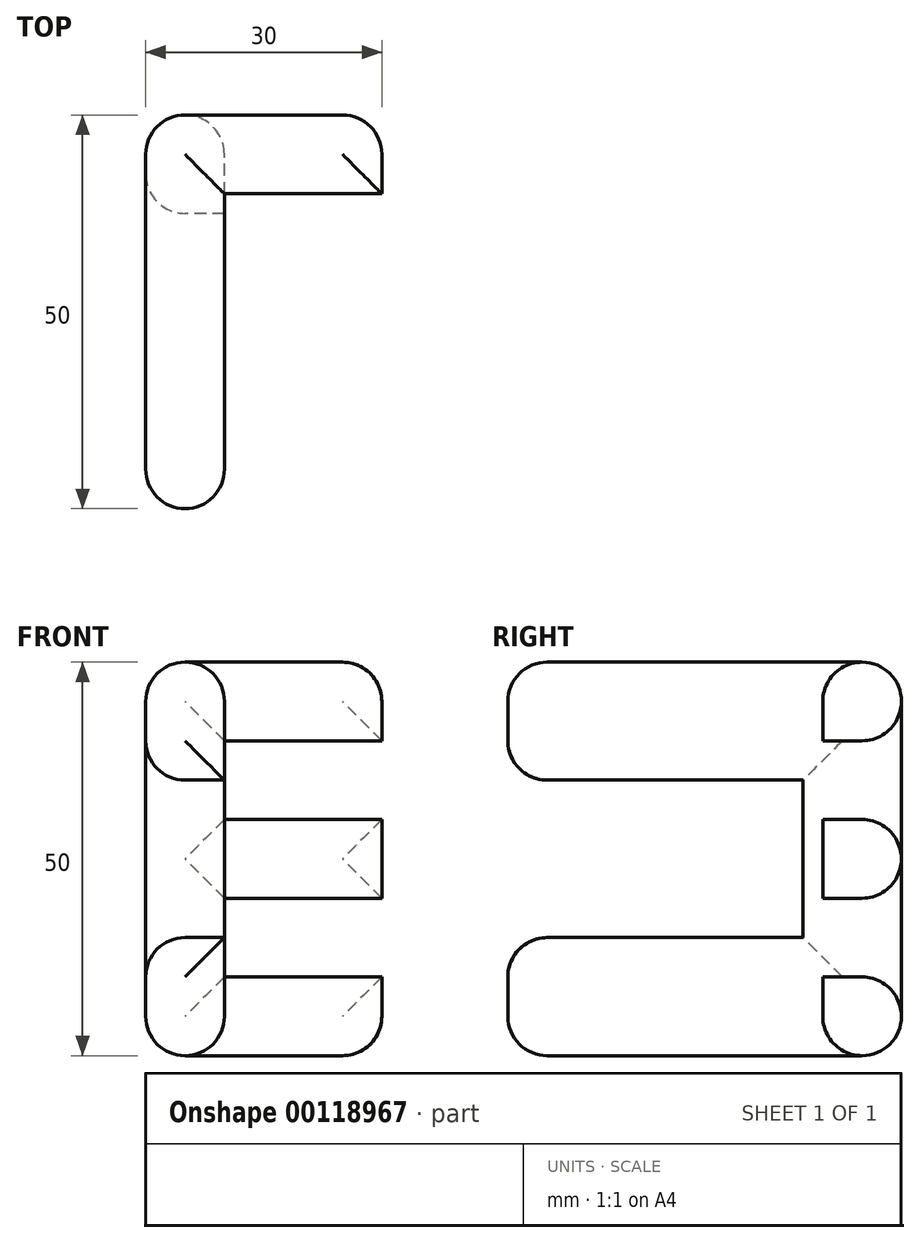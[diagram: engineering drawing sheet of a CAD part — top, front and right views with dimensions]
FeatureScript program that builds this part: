
annotation { "Feature Type Name" : "Feature", "Feature Type Description" : "" }
export const myFeature = defineFeature(function(context is Context, id is Id, definition is map)
    precondition{}
    {
        {
            var Q0;
            Q0=qCreatedBy(makeId("Front.planeOp"),FACE);
            var sketch = newSketch(context, id + "F0", { "sketchPlane" : qUnion([Q0])});
            skLineSegment(sketch, "E0.bottom", {"start": v(25, 25) * mm, "end": v(-25, 25) * mm, "construction": true});
            skLineSegment(sketch, "E0.top", {"start": v(25, -25) * mm, "end": v(-25, -25) * mm, "construction": true});
            skLineSegment(sketch, "E0.left", {"start": v(25, 25) * mm, "end": v(25, -25) * mm, "construction": true});
            skLineSegment(sketch, "E0.right", {"start": v(-25, 25) * mm, "end": v(-25, -25) * mm, "construction": true});
            skPoint(sketch, "E0.middle", {"position": v(0, 0) * mm});
            skLineSegment(sketch, "E1", {"start": v(-15, 25) * mm, "end": v(-15, -25) * mm, "construction": true});
            skLineSegment(sketch, "E2", {"start": v(-5, 25) * mm, "end": v(-5, -25) * mm, "construction": true});
            skLineSegment(sketch, "E3", {"start": v(5, 25) * mm, "end": v(5, -25) * mm, "construction": true});
            skLineSegment(sketch, "E4", {"start": v(15, 25) * mm, "end": v(15, -25) * mm, "construction": true});
            skLineSegment(sketch, "E5", {"start": v(-25, 15) * mm, "end": v(25, 15) * mm, "construction": true});
            skLineSegment(sketch, "E6", {"start": v(-25, 5) * mm, "end": v(25, 5) * mm, "construction": true});
            skLineSegment(sketch, "E7", {"start": v(-25, -5) * mm, "end": v(25, -5) * mm, "construction": true});
            skLineSegment(sketch, "E8", {"start": v(-25, -15) * mm, "end": v(25, -15) * mm, "construction": true});
            skLineSegment(sketch, "E9", {"start": v(-15, 25) * mm, "end": v(-15, -25) * mm});
            skLineSegment(sketch, "E10", {"start": v(15, -25) * mm, "end": v(15, -15) * mm});
            skLineSegment(sketch, "E11", {"start": v(15, -15) * mm, "end": v(-5, -15) * mm});
            skLineSegment(sketch, "E12", {"start": v(-5, -15) * mm, "end": v(-5, -5) * mm});
            skLineSegment(sketch, "E13", {"start": v(-5, -5) * mm, "end": v(15, -5) * mm});
            skLineSegment(sketch, "E14", {"start": v(15, -5) * mm, "end": v(15, 5) * mm});
            skLineSegment(sketch, "E15", {"start": v(15, 5) * mm, "end": v(-5, 5) * mm});
            skLineSegment(sketch, "E16", {"start": v(-5, 5) * mm, "end": v(-5, 15) * mm});
            skLineSegment(sketch, "E17", {"start": v(-5, 15) * mm, "end": v(15, 15) * mm});
            skLineSegment(sketch, "E18", {"start": v(15, 15) * mm, "end": v(15, 25) * mm});
            skLineSegment(sketch, "E19", {"start": v(15, 25) * mm, "end": v(-15, 25) * mm});
            skLineSegment(sketch, "E20", {"start": v(15, -25) * mm, "end": v(-15, -25) * mm});
            skSolve(sketch);
        }
        {
            var Q0;
            Q0=qCreatedBy(makeId("Top.planeOp"),FACE);
            var sketch = newSketch(context, id + "F1", { "sketchPlane" : qUnion([Q0])});
            skLineSegment(sketch, "E21.bottom", {"start": v(25, -25) * mm, "end": v(-25, -25) * mm, "construction": true});
            skLineSegment(sketch, "E21.top", {"start": v(25, 25) * mm, "end": v(-25, 25) * mm, "construction": true});
            skLineSegment(sketch, "E21.left", {"start": v(25, -25) * mm, "end": v(25, 25) * mm, "construction": true});
            skLineSegment(sketch, "E21.right", {"start": v(-25, -25) * mm, "end": v(-25, 25) * mm, "construction": true});
            skPoint(sketch, "E21.middle", {"position": v(0, 0) * mm});
            skLineSegment(sketch, "E22", {"start": v(-15, -25) * mm, "end": v(-15, 25) * mm});
            skLineSegment(sketch, "E23", {"start": v(-15, 25) * mm, "end": v(15, 25) * mm});
            skLineSegment(sketch, "E24", {"start": v(15, 25) * mm, "end": v(15, 15) * mm});
            skLineSegment(sketch, "E25", {"start": v(15, 15) * mm, "end": v(-5, 15) * mm});
            skLineSegment(sketch, "E26", {"start": v(-5, 15) * mm, "end": v(-5, -25) * mm});
            skLineSegment(sketch, "E27", {"start": v(-5, -25) * mm, "end": v(-15, -25) * mm});
            skSolve(sketch);
        }
        {
            var Q0;
            Q0=qCreatedBy(makeId("Right.planeOp"),FACE);
            var sketch = newSketch(context, id + "F2", { "sketchPlane" : qUnion([Q0])});
            skLineSegment(sketch, "E28.bottom", {"start": v(-25, 25) * mm, "end": v(25, 25) * mm, "construction": true});
            skLineSegment(sketch, "E28.top", {"start": v(-25, -25) * mm, "end": v(25, -25) * mm, "construction": true});
            skLineSegment(sketch, "E28.left", {"start": v(-25, 25) * mm, "end": v(-25, -25) * mm, "construction": true});
            skLineSegment(sketch, "E28.right", {"start": v(25, 8.65) * mm, "end": v(25, -8.65) * mm, "construction": true});
            skPoint(sketch, "E28.middle", {"position": v(0, 0) * mm});
            skLineSegment(sketch, "E29", {"start": v(25, -15) * mm, "end": v(25, 15) * mm});
            skLineSegment(sketch, "E30", {"start": v(-25, 15) * mm, "end": v(-25, 5) * mm});
            skLineSegment(sketch, "E31", {"start": v(-25, -5) * mm, "end": v(-25, -15) * mm});
            skLineSegment(sketch, "E32", {"start": v(-25, -25) * mm, "end": v(25, -25) * mm});
            skLineSegment(sketch, "E33", {"start": v(25, -25) * mm, "end": v(25, -8.65) * mm});
            skLineSegment(sketch, "E34", {"start": v(25, 8.65) * mm, "end": v(25, 25) * mm});
            skLineSegment(sketch, "E35", {"start": v(25, 25) * mm, "end": v(-25, 25) * mm});
            skLineSegment(sketch, "E36", {"start": v(-25, 25) * mm, "end": v(-25, 15) * mm});
            skLineSegment(sketch, "E37", {"start": v(25, 25) * mm, "end": v(25, -25) * mm});
            skLineSegment(sketch, "E38", {"start": v(-25, -25) * mm, "end": v(-25, -10) * mm});
            skLineSegment(sketch, "E39", {"start": v(-25, 25) * mm, "end": v(-25, 10) * mm});
            skLineSegment(sketch, "E40", {"start": v(-25, 10) * mm, "end": v(12.5, 10) * mm});
            skLineSegment(sketch, "E41", {"start": v(-25, -10) * mm, "end": v(12.5, -10) * mm});
            skLineSegment(sketch, "E42", {"start": v(12.5, 10) * mm, "end": v(12.5, -10) * mm});
            skSolve(sketch);
        }
        {
            var Q0;
            Q0=makeQuery(id+"F0.imprint","IMPRINT",FACE,{"disambiguationData":[TD([[makeQuery(id+"F0.imprint","IMPRINT",EDGE,{"derivedFrom":sQuery(id+"F0.wireOp",EDGE,"E10")}),1.0]])]});
            extrude(context, id + "F3", {"entities" : qUnion([Q0]), "endBound" : BoundingType.SYMMETRIC, "depth" : 50 * mm});
        }
        {
            var Q0;
            Q0=makeQuery(id+"F1.imprint","IMPRINT",FACE,{"disambiguationData":[TD([[makeQuery(id+"F1.imprint","IMPRINT",EDGE,{"derivedFrom":sQuery(id+"F1.wireOp",EDGE,"E22")}),-1.0]])]});
            extrude(context, id + "F4", {"entities" : qUnion([Q0]), "operationType" : NewBodyOperationType.INTERSECT, "endBound" : BoundingType.SYMMETRIC, "depth" : 50 * mm});
        }
        {
            var Q0;
            {var subQ2=sQuery(id+"F2.wireOp",EDGE,"E32");Q0=makeQuery(id+"F2.imprint","IMPRINT",FACE,{"disambiguationData":[TD([[makeQuery(id+"F2.imprint","IMPRINT",EDGE,{"derivedFrom":subQ2}),1.0]])]});}
            extrude(context, id + "F5", {"entities" : qUnion([Q0]), "operationType" : NewBodyOperationType.INTERSECT, "endBound" : BoundingType.SYMMETRIC, "depth" : 50 * mm});
        }
        {
            var Q0;
            Q0=makeQuery(id+"F3.opExtrude","SWEPT_FACE",FACE,{"disambiguationData":[OSD([sQuery(id+"F0.wireOp",EDGE,"E9")])]});
            fillet(context, id + "F6", {"entities" : qUnion([Q0]), "radius" : 5 * mm, "tangentPropagation" : true, "allowEdgeOverflow" : false});
        }
        {
            var Q0;
            Q0=makeQuery(id+"F3.opExtrude","SWEPT_FACE",FACE,{"disambiguationData":[OSD([sQuery(id+"F0.wireOp",EDGE,"E19")])]});
            fillet(context, id + "F7", {"entities" : qUnion([Q0]), "radius" : 5 * mm, "tangentPropagation" : true, "allowEdgeOverflow" : false});
        }
        {
            var Q0;
            Q0=makeQuery(id+"F3.opExtrude","SWEPT_FACE",FACE,{"disambiguationData":[OSD([sQuery(id+"F0.wireOp",EDGE,"E20")])]});
            fillet(context, id + "F8", {"entities" : qUnion([Q0]), "radius" : 5 * mm, "tangentPropagation" : true, "allowEdgeOverflow" : false});
        }
        {
            var Q0;
            Q0=makeQuery(id+"F3.opExtrude","CAP_FACE",FACE,{"disambiguationData":[OSD([sQuery(id+"F0.wireOp",EDGE,"E10"),sQuery(id+"F0.wireOp",EDGE,"E11"),sQuery(id+"F0.wireOp",EDGE,"E12"),sQuery(id+"F0.wireOp",EDGE,"E13"),sQuery(id+"F0.wireOp",EDGE,"E14"),sQuery(id+"F0.wireOp",EDGE,"E15"),sQuery(id+"F0.wireOp",EDGE,"E16"),sQuery(id+"F0.wireOp",EDGE,"E17"),sQuery(id+"F0.wireOp",EDGE,"E18"),sQuery(id+"F0.wireOp",EDGE,"E19"),sQuery(id+"F0.wireOp",EDGE,"E9"),sQuery(id+"F0.wireOp",EDGE,"E20")])],"isStart":true});
            fillet(context, id + "F9", {"entities" : qUnion([Q0]), "radius" : 5 * mm, "tangentPropagation" : true, "allowEdgeOverflow" : false});
        }
        {
            var Q0;
            {var subQ0=sQuery(id+"F0.wireOp",EDGE,"E20");var subQ1=sQuery(id+"F0.wireOp",EDGE,"E12");var subQ2=sQuery(id+"F0.wireOp",EDGE,"E9");var subQ3=sQuery(id+"F0.wireOp",EDGE,"E16");Q0=makeQuery(id+"F5.boolean.opBoolean","SPLIT",FACE,{"disambiguationData":[TD([makeQuery(id+"F3.opExtrude","SWEPT_FACE",FACE,{"disambiguationData":[OSD([subQ0])]})])],"derivedFrom":makeQuery(id+"F3.opExtrude","CAP_FACE",FACE,{"disambiguationData":[OSD([sQuery(id+"F0.wireOp",EDGE,"E10"),sQuery(id+"F0.wireOp",EDGE,"E11"),subQ1,sQuery(id+"F0.wireOp",EDGE,"E13"),sQuery(id+"F0.wireOp",EDGE,"E14"),sQuery(id+"F0.wireOp",EDGE,"E15"),subQ3,sQuery(id+"F0.wireOp",EDGE,"E17"),sQuery(id+"F0.wireOp",EDGE,"E18"),sQuery(id+"F0.wireOp",EDGE,"E19"),subQ2,subQ0])],"isStart":false})});}
            fillet(context, id + "F10", {"entities" : qUnion([Q0]), "radius" : 5 * mm, "tangentPropagation" : true, "allowEdgeOverflow" : false});
        }
        {
            var Q0;
            {var subQ0=sQuery(id+"F0.wireOp",EDGE,"E9");var subQ1=sQuery(id+"F0.wireOp",EDGE,"E19");var subQ2=sQuery(id+"F0.wireOp",EDGE,"E16");var subQ3=sQuery(id+"F0.wireOp",EDGE,"E12");Q0=makeQuery(id+"F5.boolean.opBoolean","SPLIT",FACE,{"disambiguationData":[TD([makeQuery(id+"F3.opExtrude","SWEPT_FACE",FACE,{"disambiguationData":[OSD([subQ1])]})])],"derivedFrom":makeQuery(id+"F3.opExtrude","CAP_FACE",FACE,{"disambiguationData":[OSD([sQuery(id+"F0.wireOp",EDGE,"E10"),sQuery(id+"F0.wireOp",EDGE,"E11"),subQ3,sQuery(id+"F0.wireOp",EDGE,"E13"),sQuery(id+"F0.wireOp",EDGE,"E14"),sQuery(id+"F0.wireOp",EDGE,"E15"),subQ2,sQuery(id+"F0.wireOp",EDGE,"E17"),sQuery(id+"F0.wireOp",EDGE,"E18"),subQ1,subQ0,sQuery(id+"F0.wireOp",EDGE,"E20")])],"isStart":false})});}
            fillet(context, id + "F11", {"entities" : qUnion([Q0]), "radius" : 5 * mm, "tangentPropagation" : true, "allowEdgeOverflow" : false});
        }
    });
